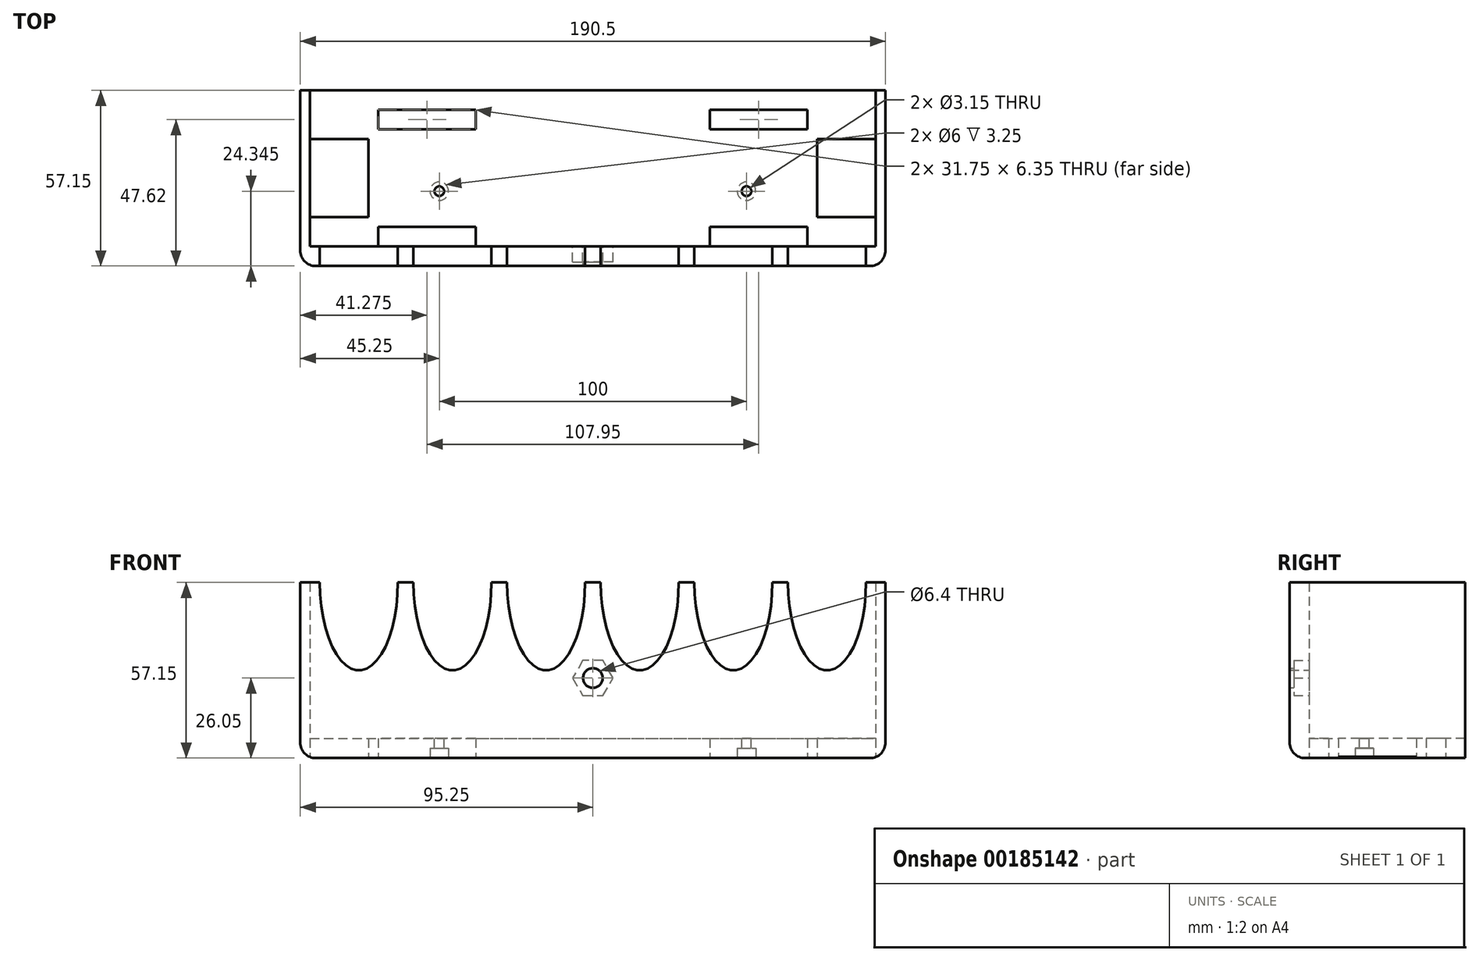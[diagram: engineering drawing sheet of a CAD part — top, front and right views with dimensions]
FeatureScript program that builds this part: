
annotation { "Feature Type Name" : "Feature", "Feature Type Description" : "" }
export const myFeature = defineFeature(function(context is Context, id is Id, definition is map)
    precondition{}
    {
        {
            var Q0;
            Q0=qCreatedBy(makeId("Top.planeOp"),FACE);
            var sketch = newSketch(context, id + "F0", { "sketchPlane" : qUnion([Q0])});
            skLineSegment(sketch, "E0.bottom", {"start": v(-95.25, -20.45) * mm, "end": v(95.25, -20.45) * mm});
            skLineSegment(sketch, "E0.top", {"start": v(-95.25, -77.6) * mm, "end": v(95.25, -77.6) * mm});
            skLineSegment(sketch, "E0.left", {"start": v(-95.25, -20.45) * mm, "end": v(-95.25, -77.6) * mm});
            skLineSegment(sketch, "E0.right", {"start": v(95.25, -20.45) * mm, "end": v(95.25, -77.6) * mm});
            skLineSegment(sketch, "E1.bottom", {"start": v(38.1, -26.8) * mm, "end": v(69.85, -26.8) * mm});
            skLineSegment(sketch, "E1.top", {"start": v(38.1, -33.15) * mm, "end": v(69.85, -33.15) * mm});
            skLineSegment(sketch, "E1.left", {"start": v(38.1, -26.8) * mm, "end": v(38.1, -33.15) * mm});
            skLineSegment(sketch, "E1.right", {"start": v(69.85, -26.8) * mm, "end": v(69.85, -33.15) * mm});
            skLineSegment(sketch, "E2.bottom", {"start": v(38.1, -64.9) * mm, "end": v(69.85, -64.9) * mm});
            skLineSegment(sketch, "E2.top", {"start": v(38.1, -71.25) * mm, "end": v(69.85, -71.25) * mm});
            skLineSegment(sketch, "E2.left", {"start": v(38.1, -64.9) * mm, "end": v(38.1, -71.25) * mm});
            skLineSegment(sketch, "E2.right", {"start": v(69.85, -64.9) * mm, "end": v(69.85, -71.25) * mm});
            skLineSegment(sketch, "E3", {"start": v(0, -20.45) * mm, "end": v(0, -77.6) * mm, "construction": true});
            skLineSegment(sketch, "E4.MirrorCS", {"start": v(-38.1, -26.8) * mm, "end": v(-38.1, -33.15) * mm});
            skLineSegment(sketch, "E5.MirrorCS", {"start": v(-38.1, -26.8) * mm, "end": v(-69.85, -26.8) * mm});
            skLineSegment(sketch, "E6.MirrorCS", {"start": v(-69.85, -26.8) * mm, "end": v(-69.85, -33.15) * mm});
            skLineSegment(sketch, "E7.MirrorCS", {"start": v(-38.1, -33.15) * mm, "end": v(-69.85, -33.15) * mm});
            skLineSegment(sketch, "E8.MirrorCS", {"start": v(-38.1, -64.9) * mm, "end": v(-69.85, -64.9) * mm});
            skLineSegment(sketch, "E9.MirrorCS", {"start": v(-69.85, -64.9) * mm, "end": v(-69.85, -71.25) * mm});
            skLineSegment(sketch, "E10.MirrorCS", {"start": v(-38.1, -71.25) * mm, "end": v(-69.85, -71.25) * mm});
            skLineSegment(sketch, "E11.MirrorCS", {"start": v(-38.1, -64.9) * mm, "end": v(-38.1, -71.25) * mm});
            skSolve(sketch);
        }
        {
            var Q0;
            Q0 = qSketchRegion(id + "F0", true);
            extrude(context, id + "F1", {"entities" : qUnion([Q0]), "depth" : 6.35 * mm});
        }
        {
            var Q0;
            Q0=makeQuery(id+"F1.opExtrude","CAP_FACE",FACE,{"disambiguationData":[OSD([sQuery(id+"F0.wireOp",EDGE,"E0.bottom"),sQuery(id+"F0.wireOp",EDGE,"E0.top"),sQuery(id+"F0.wireOp",EDGE,"E0.left"),sQuery(id+"F0.wireOp",EDGE,"E0.right"),sQuery(id+"F0.wireOp",EDGE,"E1.bottom"),sQuery(id+"F0.wireOp",EDGE,"E1.top"),sQuery(id+"F0.wireOp",EDGE,"E1.left"),sQuery(id+"F0.wireOp",EDGE,"E1.right"),sQuery(id+"F0.wireOp",EDGE,"E2.bottom"),sQuery(id+"F0.wireOp",EDGE,"E2.top"),sQuery(id+"F0.wireOp",EDGE,"E2.left"),sQuery(id+"F0.wireOp",EDGE,"E2.right"),sQuery(id+"F0.wireOp",EDGE,"E4.MirrorCS"),sQuery(id+"F0.wireOp",EDGE,"E5.MirrorCS"),sQuery(id+"F0.wireOp",EDGE,"E6.MirrorCS"),sQuery(id+"F0.wireOp",EDGE,"E7.MirrorCS"),sQuery(id+"F0.wireOp",EDGE,"E8.MirrorCS"),sQuery(id+"F0.wireOp",EDGE,"E9.MirrorCS"),sQuery(id+"F0.wireOp",EDGE,"E10.MirrorCS"),sQuery(id+"F0.wireOp",EDGE,"E11.MirrorCS")])],"isStart":false});
            var sketch = newSketch(context, id + "F2", { "sketchPlane" : qUnion([Q0])});
            skLineSegment(sketch, "E12", {"start": v(-95.25, -20.45) * mm, "end": v(-95.25, -77.6) * mm});
            skLineSegment(sketch, "E13", {"start": v(-95.25, -77.6) * mm, "end": v(95.25, -77.6) * mm});
            skLineSegment(sketch, "E14", {"start": v(95.25, -77.6) * mm, "end": v(95.25, -20.45) * mm});
            skLineSegment(sketch, "E15", {"start": v(95.25, -20.45) * mm, "end": v(92.08, -20.45) * mm});
            skLineSegment(sketch, "E16", {"start": v(92.08, -20.45) * mm, "end": v(92.08, -71.25) * mm});
            skLineSegment(sketch, "E17", {"start": v(92.07, -71.25) * mm, "end": v(-92.08, -71.25) * mm});
            skPoint(sketch, "E17.endSnap0", {"position": v(53.98, -71.25) * mm});
            skLineSegment(sketch, "E18", {"start": v(-92.08, -71.25) * mm, "end": v(-92.08, -20.45) * mm});
            skLineSegment(sketch, "E19", {"start": v(-92.08, -20.45) * mm, "end": v(-95.25, -20.45) * mm});
            skSolve(sketch);
        }
        {
            var Q0;
            Q0 = qSketchRegion(id + "F2", true);
            extrude(context, id + "F3", {"entities" : qUnion([Q0]), "operationType" : NewBodyOperationType.ADD, "depth" : 50.8 * mm});
        }
        {
            var Q0;
            Q0=makeQuery(id+"F1.opExtrude","CAP_FACE",FACE,{"disambiguationData":[OSD([sQuery(id+"F0.wireOp",EDGE,"E0.bottom"),sQuery(id+"F0.wireOp",EDGE,"E0.top"),sQuery(id+"F0.wireOp",EDGE,"E0.left"),sQuery(id+"F0.wireOp",EDGE,"E0.right"),sQuery(id+"F0.wireOp",EDGE,"E1.bottom"),sQuery(id+"F0.wireOp",EDGE,"E1.top"),sQuery(id+"F0.wireOp",EDGE,"E1.left"),sQuery(id+"F0.wireOp",EDGE,"E1.right"),sQuery(id+"F0.wireOp",EDGE,"E2.bottom"),sQuery(id+"F0.wireOp",EDGE,"E2.top"),sQuery(id+"F0.wireOp",EDGE,"E2.left"),sQuery(id+"F0.wireOp",EDGE,"E2.right"),sQuery(id+"F0.wireOp",EDGE,"E4.MirrorCS"),sQuery(id+"F0.wireOp",EDGE,"E5.MirrorCS"),sQuery(id+"F0.wireOp",EDGE,"E6.MirrorCS"),sQuery(id+"F0.wireOp",EDGE,"E7.MirrorCS"),sQuery(id+"F0.wireOp",EDGE,"E8.MirrorCS"),sQuery(id+"F0.wireOp",EDGE,"E9.MirrorCS"),sQuery(id+"F0.wireOp",EDGE,"E10.MirrorCS"),sQuery(id+"F0.wireOp",EDGE,"E11.MirrorCS")])],"isStart":false});
            var sketch = newSketch(context, id + "F4", { "sketchPlane" : qUnion([Q0])});
            skCircle(sketch, "E20", {"center": v(-50, -53.25) * mm, "radius": 1.57 * mm});
            skCircle(sketch, "E21", {"center": v(50, -53.25) * mm, "radius": 1.57 * mm});
            skLineSegment(sketch, "E22", {"start": v(-50, -53.25) * mm, "end": v(50, -53.25) * mm, "construction": true});
            skPoint(sketch, "E23", {"position": v(0, -53.25) * mm});
            skSolve(sketch);
        }
        {
            var Q0;
            Q0 = qSketchRegion(id + "F4", true);
            extrude(context, id + "F5", {"entities" : qUnion([Q0]), "operationType" : NewBodyOperationType.REMOVE, "oppositeDirection" : true, "depth" : 25.4 * mm});
        }
        {
            var Q0;
            Q0=makeQuery(id+"F1.opExtrude","CAP_FACE",FACE,{"disambiguationData":[OSD([sQuery(id+"F0.wireOp",EDGE,"E0.bottom"),sQuery(id+"F0.wireOp",EDGE,"E0.top"),sQuery(id+"F0.wireOp",EDGE,"E0.left"),sQuery(id+"F0.wireOp",EDGE,"E0.right"),sQuery(id+"F0.wireOp",EDGE,"E1.bottom"),sQuery(id+"F0.wireOp",EDGE,"E1.top"),sQuery(id+"F0.wireOp",EDGE,"E1.left"),sQuery(id+"F0.wireOp",EDGE,"E1.right"),sQuery(id+"F0.wireOp",EDGE,"E2.bottom"),sQuery(id+"F0.wireOp",EDGE,"E2.top"),sQuery(id+"F0.wireOp",EDGE,"E2.left"),sQuery(id+"F0.wireOp",EDGE,"E2.right"),sQuery(id+"F0.wireOp",EDGE,"E4.MirrorCS"),sQuery(id+"F0.wireOp",EDGE,"E5.MirrorCS"),sQuery(id+"F0.wireOp",EDGE,"E6.MirrorCS"),sQuery(id+"F0.wireOp",EDGE,"E7.MirrorCS"),sQuery(id+"F0.wireOp",EDGE,"E8.MirrorCS"),sQuery(id+"F0.wireOp",EDGE,"E9.MirrorCS"),sQuery(id+"F0.wireOp",EDGE,"E10.MirrorCS"),sQuery(id+"F0.wireOp",EDGE,"E11.MirrorCS")])],"isStart":true});
            var sketch = newSketch(context, id + "F6", { "sketchPlane" : qUnion([Q0])});
            skCircle(sketch, "E24", {"center": v(-50, 53.25) * mm, "radius": 3 * mm});
            skCircle(sketch, "E25", {"center": v(50, 53.25) * mm, "radius": 3 * mm});
            skSolve(sketch);
        }
        {
            var Q0;
            Q0 = qSketchRegion(id + "F6", true);
            extrude(context, id + "F7", {"entities" : qUnion([Q0]), "operationType" : NewBodyOperationType.REMOVE, "oppositeDirection" : true, "depth" : 3.25 * mm});
        }
        {
            var Q0;
            Q0=makeQuery(id+"F3.boolean.opBoolean","MERGE",FACE,{"derivedFrom":[makeQuery(id+"F1.opExtrude","SWEPT_FACE",FACE,{"disambiguationData":[OSD([sQuery(id+"F0.wireOp",EDGE,"E2.top")])]}),makeQuery(id+"F1.opExtrude","SWEPT_FACE",FACE,{"disambiguationData":[OSD([sQuery(id+"F0.wireOp",EDGE,"E10.MirrorCS")])]}),makeQuery(id+"F3.opExtrude","SWEPT_FACE",FACE,{"disambiguationData":[OSD([sQuery(id+"F2.wireOp",EDGE,"E17")])]})]});
            var sketch = newSketch(context, id + "F8", { "sketchPlane" : qUnion([Q0])});
            skCircle(sketch, "E26.cCircle", {"center": v(0, 26.05) * mm, "radius": 5.7 * mm, "construction": true});
            skLineSegment(sketch, "E26.0", {"start": v(6.58, 26.05) * mm, "end": v(3.3, 20.35) * mm});
            skLineSegment(sketch, "E26.1", {"start": v(3.3, 20.35) * mm, "end": v(-3.3, 20.35) * mm});
            skLineSegment(sketch, "E26.2", {"start": v(-3.3, 20.35) * mm, "end": v(-6.58, 26.05) * mm});
            skLineSegment(sketch, "E26.3", {"start": v(-6.58, 26.05) * mm, "end": v(-3.3, 31.75) * mm});
            skLineSegment(sketch, "E26.4", {"start": v(-3.3, 31.75) * mm, "end": v(3.3, 31.75) * mm});
            skLineSegment(sketch, "E26.5", {"start": v(3.3, 31.75) * mm, "end": v(6.58, 26.05) * mm});
            skPoint(sketch, "E26.0.midPoint", {"position": v(4.94, 23.2) * mm});
            skLineSegment(sketch, "E27", {"start": v(0, 57.15) * mm, "end": v(0, 6.35) * mm, "construction": true});
            skSolve(sketch);
        }
        {
            var Q0;
            Q0 = qSketchRegion(id + "F8", true);
            extrude(context, id + "F9", {"entities" : qUnion([Q0]), "operationType" : NewBodyOperationType.REMOVE, "oppositeDirection" : true, "depth" : 5 * mm});
        }
        {
            var Q0;
            Q0=makeQuery(id+"F9.boolean.opBoolean","COPY",FACE,{"derivedFrom":makeQuery(id+"F9.opExtrude","CAP_FACE",FACE,{"disambiguationData":[OSD([sQuery(id+"F8.wireOp",EDGE,"E26.0"),sQuery(id+"F8.wireOp",EDGE,"E26.1"),sQuery(id+"F8.wireOp",EDGE,"E26.2"),sQuery(id+"F8.wireOp",EDGE,"E26.3"),sQuery(id+"F8.wireOp",EDGE,"E26.4"),sQuery(id+"F8.wireOp",EDGE,"E26.5")])],"isStart":false})});
            var sketch = newSketch(context, id + "F10", { "sketchPlane" : qUnion([Q0])});
            skLineSegment(sketch, "E28", {"start": v(0, 31.75) * mm, "end": v(0, 20.35) * mm, "construction": true});
            skCircle(sketch, "E29", {"center": v(0, 26.05) * mm, "radius": 3.2 * mm});
            skSolve(sketch);
        }
        {
            var Q0;
            Q0 = qSketchRegion(id + "F10", true);
            extrude(context, id + "F11", {"entities" : qUnion([Q0]), "operationType" : NewBodyOperationType.REMOVE, "oppositeDirection" : true, "depth" : 25.4 * mm});
        }
        {
            var Q0;
            Q0=makeQuery(id+"F1.opExtrude","CAP_FACE",FACE,{"disambiguationData":[OSD([sQuery(id+"F0.wireOp",EDGE,"E0.bottom"),sQuery(id+"F0.wireOp",EDGE,"E0.top"),sQuery(id+"F0.wireOp",EDGE,"E0.left"),sQuery(id+"F0.wireOp",EDGE,"E0.right"),sQuery(id+"F0.wireOp",EDGE,"E1.bottom"),sQuery(id+"F0.wireOp",EDGE,"E1.top"),sQuery(id+"F0.wireOp",EDGE,"E1.left"),sQuery(id+"F0.wireOp",EDGE,"E1.right"),sQuery(id+"F0.wireOp",EDGE,"E2.bottom"),sQuery(id+"F0.wireOp",EDGE,"E2.top"),sQuery(id+"F0.wireOp",EDGE,"E2.left"),sQuery(id+"F0.wireOp",EDGE,"E2.right"),sQuery(id+"F0.wireOp",EDGE,"E4.MirrorCS"),sQuery(id+"F0.wireOp",EDGE,"E5.MirrorCS"),sQuery(id+"F0.wireOp",EDGE,"E6.MirrorCS"),sQuery(id+"F0.wireOp",EDGE,"E7.MirrorCS"),sQuery(id+"F0.wireOp",EDGE,"E8.MirrorCS"),sQuery(id+"F0.wireOp",EDGE,"E9.MirrorCS"),sQuery(id+"F0.wireOp",EDGE,"E10.MirrorCS"),sQuery(id+"F0.wireOp",EDGE,"E11.MirrorCS")])],"isStart":true});
            var sketch = newSketch(context, id + "F12", { "sketchPlane" : qUnion([Q0])});
            skLineSegment(sketch, "E30.bottom", {"start": v(-73.03, 61.73) * mm, "end": v(-92.08, 61.73) * mm});
            skLineSegment(sketch, "E30.top", {"start": v(-73.03, 36.33) * mm, "end": v(-92.08, 36.33) * mm});
            skLineSegment(sketch, "E30.left", {"start": v(-73.03, 61.73) * mm, "end": v(-73.03, 36.33) * mm});
            skLineSegment(sketch, "E30.right", {"start": v(-92.08, 61.73) * mm, "end": v(-92.08, 36.33) * mm});
            skLineSegment(sketch, "E31", {"start": v(-95.25, 49.03) * mm, "end": v(95.25, 49.03) * mm, "construction": true});
            skPoint(sketch, "E32", {"position": v(-73.03, 49.03) * mm});
            skLineSegment(sketch, "E33.MirrorCS", {"start": v(73.03, 61.73) * mm, "end": v(73.03, 36.33) * mm});
            skLineSegment(sketch, "E34.MirrorCS", {"start": v(73.03, 61.73) * mm, "end": v(92.08, 61.73) * mm});
            skLineSegment(sketch, "E35.MirrorCS", {"start": v(92.08, 61.73) * mm, "end": v(92.08, 36.33) * mm});
            skLineSegment(sketch, "E36.MirrorCS", {"start": v(73.03, 36.33) * mm, "end": v(92.08, 36.33) * mm});
            skSolve(sketch);
        }
        {
            var Q0;
            Q0 = qSketchRegion(id + "F12", true);
            extrude(context, id + "F13", {"entities" : qUnion([Q0]), "operationType" : NewBodyOperationType.REMOVE, "oppositeDirection" : true, "depth" : 25.4 * mm});
        }
        {
            var Q0;
            Q0=makeQuery(id+"F1.opExtrude","CAP_EDGE",EDGE,{"disambiguationData":[OSD([sQuery(id+"F0.wireOp",EDGE,"E0.left")])],"isStart":true});
            var Q1;
            Q1=makeQuery(id+"F3.boolean.opBoolean","MERGE",EDGE,{"derivedFrom":[makeQuery(id+"F1.opExtrude","SWEPT_EDGE",EDGE,{"disambiguationData":[OSD([sQuery(id+"F0.wireOp",EDGE,"E0.top"),sQuery(id+"F0.wireOp",EDGE,"E0.left")])]}),makeQuery(id+"F3.opExtrude","SWEPT_EDGE",EDGE,{"disambiguationData":[OSD([sQuery(id+"F2.wireOp",EDGE,"E12"),sQuery(id+"F2.wireOp",EDGE,"E13")])]})]});
            var Q2;
            Q2=makeQuery(id+"F1.opExtrude","CAP_EDGE",EDGE,{"disambiguationData":[OSD([sQuery(id+"F0.wireOp",EDGE,"E0.top")])],"isStart":true});
            var Q3;
            Q3=makeQuery(id+"F1.opExtrude","CAP_EDGE",EDGE,{"disambiguationData":[OSD([sQuery(id+"F0.wireOp",EDGE,"E0.right")])],"isStart":true});
            var Q4;
            Q4=makeQuery(id+"F3.boolean.opBoolean","MERGE",EDGE,{"derivedFrom":[makeQuery(id+"F1.opExtrude","SWEPT_EDGE",EDGE,{"disambiguationData":[OSD([sQuery(id+"F0.wireOp",EDGE,"E0.top"),sQuery(id+"F0.wireOp",EDGE,"E0.right")])]}),makeQuery(id+"F3.opExtrude","SWEPT_EDGE",EDGE,{"disambiguationData":[OSD([sQuery(id+"F2.wireOp",EDGE,"E13"),sQuery(id+"F2.wireOp",EDGE,"E14")])]})]});
            fillet(context, id + "F14", {"entities" : qUnion([Q0, Q1, Q2, Q3, Q4]), "radius" : 5.08 * mm, "tangentPropagation" : true, "allowEdgeOverflow" : false});
        }
        {
            var Q0;
            Q0=makeQuery(id+"F3.boolean.opBoolean","MERGE",FACE,{"derivedFrom":[makeQuery(id+"F1.opExtrude","SWEPT_FACE",FACE,{"disambiguationData":[OSD([sQuery(id+"F0.wireOp",EDGE,"E2.top")])]}),makeQuery(id+"F1.opExtrude","SWEPT_FACE",FACE,{"disambiguationData":[OSD([sQuery(id+"F0.wireOp",EDGE,"E10.MirrorCS")])]}),makeQuery(id+"F3.opExtrude","SWEPT_FACE",FACE,{"disambiguationData":[OSD([sQuery(id+"F2.wireOp",EDGE,"E17")])]})]});
            var sketch = newSketch(context, id + "F15", { "sketchPlane" : qUnion([Q0])});
            skEllipse(sketch, "E37", {"center": v(-76.2, 57.15) * mm, "majorRadius": 28.58 * mm, "minorRadius": 12.7 * mm, "majorAxis": v(0, -1)});
            skEllipse(sketch, "E38.1.0.0", {"center": v(-45.72, 57.15) * mm, "majorRadius": 28.58 * mm, "minorRadius": 12.7 * mm, "majorAxis": v(0, -1)});
            skEllipse(sketch, "E38.2.0.0", {"center": v(-15.24, 57.15) * mm, "majorRadius": 28.58 * mm, "minorRadius": 12.7 * mm, "majorAxis": v(0, -1)});
            skEllipse(sketch, "E38.3.0.0", {"center": v(15.24, 57.15) * mm, "majorRadius": 28.58 * mm, "minorRadius": 12.7 * mm, "majorAxis": v(0, -1)});
            skEllipse(sketch, "E38.4.0.0", {"center": v(45.72, 57.15) * mm, "majorRadius": 28.58 * mm, "minorRadius": 12.7 * mm, "majorAxis": v(0, -1)});
            skLineSegment(sketch, "E38.direction1", {"start": v(-76.2, 57.15) * mm, "end": v(-45.72, 57.15) * mm, "construction": true});
            skEllipse(sketch, "E39.0.5.0", {"center": v(76.2, 57.15) * mm, "majorRadius": 28.58 * mm, "minorRadius": 12.7 * mm, "majorAxis": v(0, -1)});
            skLineSegment(sketch, "E40", {"start": v(-15.24, 57.15) * mm, "end": v(15.24, 57.15) * mm, "construction": true});
            skPoint(sketch, "E41", {"position": v(0, 57.15) * mm});
            skSolve(sketch);
        }
        {
            var Q0;
            Q0 = qSketchRegion(id + "F15", true);
            extrude(context, id + "F16", {"entities" : qUnion([Q0]), "operationType" : NewBodyOperationType.REMOVE, "endBound" : BoundingType.THROUGH_ALL, "oppositeDirection" : true, "depth" : 25.4 * mm});
        }
    });
